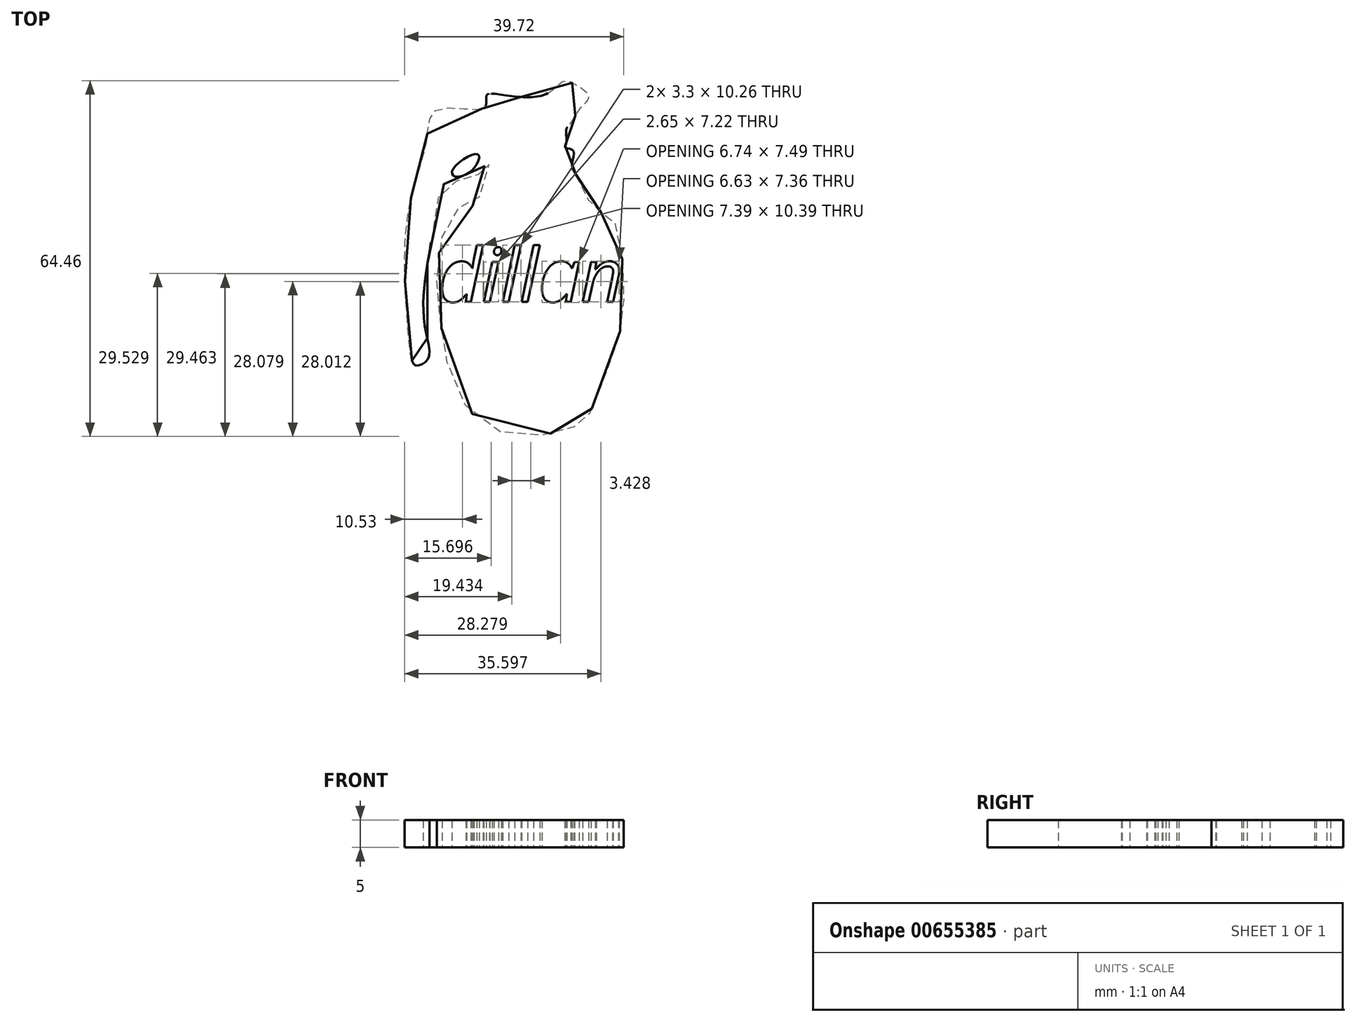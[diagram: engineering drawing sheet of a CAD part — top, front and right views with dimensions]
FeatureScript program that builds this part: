
annotation { "Feature Type Name" : "Feature", "Feature Type Description" : "" }
export const myFeature = defineFeature(function(context is Context, id is Id, definition is map)
    precondition{}
    {
        {
            var Q0;
            Q0=qCreatedBy(makeId("Top.planeOp"),FACE);
            var sketch = newSketch(context, id + "F0", { "sketchPlane" : qUnion([Q0])});
            skFitSpline(sketch, "E0", {"points": [v(-22.5, 54.04) * mm, v(-20.55, 50.16) * mm, v(-18.97, 47.52) * mm, v(-17.38, 47.16) * mm, v(-16.32, 46.99) * mm, v(-14.38, 40.81) * mm, v(-13.85, 32.14) * mm, v(-14.73, 24.75) * mm, v(-18.44, 14.7) * mm, v(-21.26, 8.87) * mm, v(-23.03, 8.34) * mm, v(-29.2, 6.76) * mm, v(-39.43, 9.05) * mm, v(-45.61, 19.28) * mm, v(-47.37, 30.75) * mm, v(-47.55, 37.99) * mm, v(-44.38, 47.87) * mm, v(-41.9, 48.05) * mm, v(-38.55, 53.52) * mm, v(-38.38, 56.34) * mm, v(-39.79, 54.57) * mm, v(-42.61, 52.63) * mm, v(-45.96, 52.8) * mm, v(-48.26, 44.87) * mm, v(-49.85, 34.99) * mm, v(-49.85, 26.52) * mm, v(-49.14, 21.05) * mm, v(-50.55, 19.64) * mm, v(-51.79, 19.64) * mm, v(-52.84, 25.28) * mm, v(-53.55, 36.58) * mm, v(-52.84, 47.34) * mm, v(-51.08, 54.57) * mm, v(-49.5, 60.75) * mm, v(-47.55, 65.87) * mm, v(-39.08, 66.22) * mm, v(-38.73, 68.34) * mm, v(-36.96, 68.69) * mm, v(-28.32, 68.51) * mm, v(-24.79, 70.98) * mm, v(-23.03, 70.63) * mm, v(-20.2, 68.34) * mm, v(-21.61, 66.22) * mm, v(-23.03, 64.1) * mm, v(-23.9, 62.87) * mm, v(-24.26, 62.16) * mm, v(-24.26, 59.87) * mm, v(-24.44, 58.99) * mm, v(-23.03, 58.46) * mm, v(-23.2, 55.99) * mm, v(-22.5, 54.04) * mm]});
            skFitSpline(sketch, "E1", {"points": [v(-40.06, 57.55) * mm, v(-41.58, 57.58) * mm, v(-44.94, 54.72) * mm, v(-44.54, 53.78) * mm, v(-43.13, 53.83) * mm, v(-40.92, 55.32) * mm, v(-40.06, 57.55) * mm]});
            skText(sketch, "E2", { "text": "dillan\n", "fontName": "OpenSans-Italic.ttf"});
            const initialGuessF0  = {"E2": [-0.04737, 0.03103, 1, 0, 0.00972]};
            skSetInitialGuess(sketch, initialGuessF0);
            skSolve(sketch);
        }
        {
            var Q0;
            Q0 = qSketchRegion(id + "F0", true);
            extrude(context, id + "F1", {"entities" : qUnion([Q0]), "depth" : 5 * mm, "offsetDistance" : 25.4 * mm});
        }
    });
